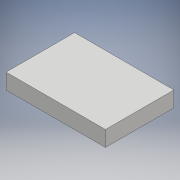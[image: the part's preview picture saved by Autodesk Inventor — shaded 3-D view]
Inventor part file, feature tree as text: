
AUTODESK INVENTOR PART (.ipt)
format: ipt  version: 2018 (Build 220112000, 112)  size: 88,576 bytes
history: native  units: mm
features: other x1, extrude x1, sketch x1
ambient origin geometry x8: Origin, YZ Plane, XZ Plane, XY Plane, X Axis, Y Axis, Z Axis, Center Point
bodies: Body1 (feature_tree)
feature tree (3):
  other  "Sólido1"
  extrude  "Extrusão1"  Depth=70.0mm
  sketch  "Esboço1"  dims[d0=101.6mm d1=70.0mm d2=15.88mm d3=0.0mm]
